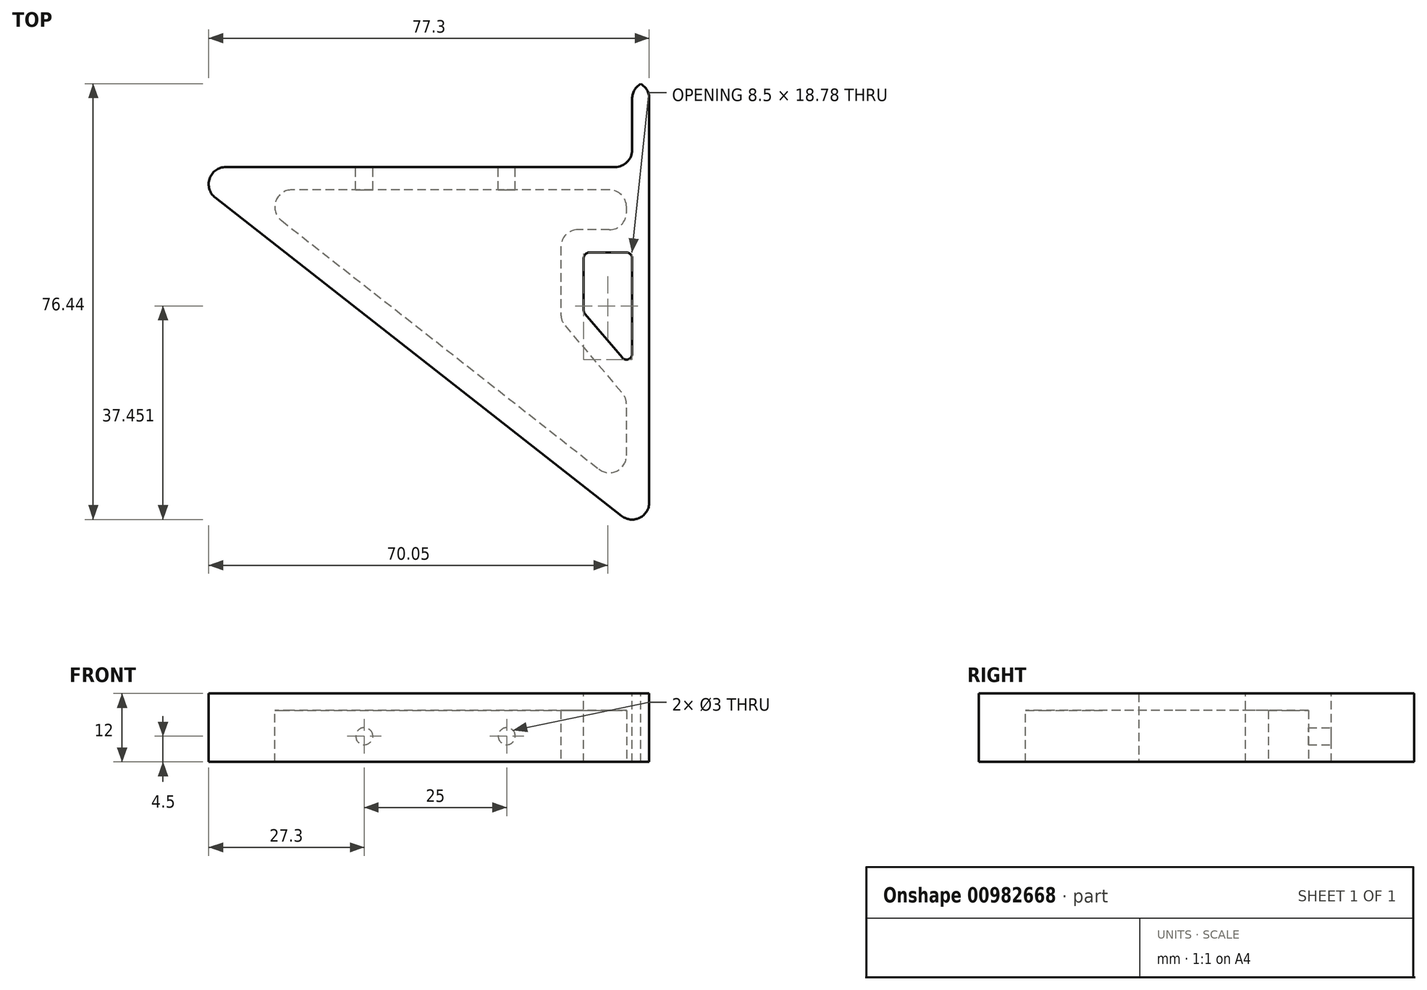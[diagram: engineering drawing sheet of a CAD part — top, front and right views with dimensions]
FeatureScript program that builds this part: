
annotation { "Feature Type Name" : "Feature", "Feature Type Description" : "" }
export const myFeature = defineFeature(function(context is Context, id is Id, definition is map)
    precondition{}
    {
        {
            var Q0;
            Q0=qCreatedBy(makeId("Top.planeOp"),FACE);
            var sketch = newSketch(context, id + "F0", { "sketchPlane" : qUnion([Q0])});
            skLineSegment(sketch, "E0", {"start": v(0, 0) * mm, "end": v(0, 80) * mm});
            skLineSegment(sketch, "E1", {"start": v(0, 80) * mm, "end": v(-3, 80) * mm});
            skLineSegment(sketch, "E2", {"start": v(-3, 80) * mm, "end": v(-3, 65) * mm});
            skLineSegment(sketch, "E3", {"start": v(-3, 65) * mm, "end": v(-83, 65) * mm});
            skLineSegment(sketch, "E4", {"start": v(-83, 65) * mm, "end": v(0, 0) * mm});
            skLineSegment(sketch, "E5", {"start": v(-3, 50) * mm, "end": v(-11.5, 50) * mm});
            skLineSegment(sketch, "E6", {"start": v(-11.5, 50) * mm, "end": v(-11.5, 39.5) * mm});
            skLineSegment(sketch, "E7", {"start": v(-11.5, 39.5) * mm, "end": v(-3, 29.5) * mm});
            skLineSegment(sketch, "E8", {"start": v(-3, 29.5) * mm, "end": v(-3, 50) * mm});
            skSolve(sketch);
        }
        {
            var Q0;
            Q0=makeQuery(id+"F0.imprint","IMPRINT",FACE,{"disambiguationData":[TD([[makeQuery(id+"F0.imprint","IMPRINT",EDGE,{"derivedFrom":sQuery(id+"F0.wireOp",EDGE,"E0")}),1.0]])]});
            extrude(context, id + "F1", {"entities" : qUnion([Q0]), "depth" : 12 * mm, "offsetDistance" : 25 * mm});
        }
        {
            var Q0;
            Q0=makeQuery(id+"F1.opExtrude","CAP_FACE",FACE,{"disambiguationData":[OSD([sQuery(id+"F0.wireOp",EDGE,"E0"),sQuery(id+"F0.wireOp",EDGE,"E1"),sQuery(id+"F0.wireOp",EDGE,"E2"),sQuery(id+"F0.wireOp",EDGE,"E3"),sQuery(id+"F0.wireOp",EDGE,"E4"),sQuery(id+"F0.wireOp",EDGE,"E5"),sQuery(id+"F0.wireOp",EDGE,"E6"),sQuery(id+"F0.wireOp",EDGE,"E7"),sQuery(id+"F0.wireOp",EDGE,"E8")])],"isStart":false});
            var sketch = newSketch(context, id + "F2", { "sketchPlane" : qUnion([Q0])});
            skLineSegment(sketch, "E9.0", {"start": v(-4, 61) * mm, "end": v(-71.4, 61) * mm});
            skLineSegment(sketch, "E10.0", {"start": v(-71.4, 61) * mm, "end": v(-4, 8.21) * mm});
            skLineSegment(sketch, "E11.0", {"start": v(-4, 54) * mm, "end": v(-15.5, 54) * mm});
            skLineSegment(sketch, "E12.0", {"start": v(-15.5, 54) * mm, "end": v(-15.5, 38.03) * mm});
            skLineSegment(sketch, "E13.0", {"start": v(-15.5, 38.03) * mm, "end": v(-4, 24.5) * mm});
            skLineSegment(sketch, "E14", {"start": v(-4, 54) * mm, "end": v(-4, 61) * mm});
            skLineSegment(sketch, "E15", {"start": v(-4, 8.21) * mm, "end": v(-4, 24.5) * mm});
            skSolve(sketch);
        }
        {
            var Q0;
            Q0=makeQuery(id+"F2.imprint","IMPRINT",FACE,{"disambiguationData":[TD([[makeQuery(id+"F2.imprint","IMPRINT",EDGE,{"derivedFrom":sQuery(id+"F2.wireOp",EDGE,"E9.0")}),1.0]])]});
            extrude(context, id + "F3", {"entities" : qUnion([Q0]), "operationType" : NewBodyOperationType.REMOVE, "oppositeDirection" : true, "depth" : 9 * mm, "offsetDistance" : 25 * mm});
        }
        {
            var Q0;
            Q0=makeQuery(id+"F1.opExtrude","SWEPT_FACE",FACE,{"disambiguationData":[OSD([sQuery(id+"F0.wireOp",EDGE,"E3")])]});
            var sketch = newSketch(context, id + "F4", { "sketchPlane" : qUnion([Q0])});
            skLineSegment(sketch, "E16", {"start": v(25, 7.5) * mm, "end": v(50, 7.5) * mm, "construction": true});
            skCircle(sketch, "E17", {"center": v(50, 7.5) * mm, "radius": 1.5 * mm});
            skCircle(sketch, "E18", {"center": v(25, 7.5) * mm, "radius": 1.5 * mm});
            skSolve(sketch);
        }
        {
            var Q0;
            Q0=qSketchRegion(id+"F4",true);
            extrude(context, id + "F5", {"entities" : qUnion([Q0]), "operationType" : NewBodyOperationType.REMOVE, "oppositeDirection" : true, "depth" : 4 * mm, "offsetDistance" : 25 * mm});
        }
        {
            var Q0;
            Q0=makeQuery(id+"F1.opExtrude","SWEPT_EDGE",EDGE,{"disambiguationData":[OSD([sQuery(id+"F0.wireOp",EDGE,"E2"),sQuery(id+"F0.wireOp",EDGE,"E3")])]});
            var Q1;
            Q1=makeQuery(id+"F3.boolean.opBoolean","COPY",EDGE,{"derivedFrom":makeQuery(id+"F3.opExtrude","SWEPT_EDGE",EDGE,{"disambiguationData":[OSD([sQuery(id+"F2.wireOp",EDGE,"E11.0"),sQuery(id+"F2.wireOp",EDGE,"E14")])]})});
            var Q2;
            Q2=makeQuery(id+"F3.boolean.opBoolean","COPY",EDGE,{"derivedFrom":makeQuery(id+"F3.opExtrude","SWEPT_EDGE",EDGE,{"disambiguationData":[OSD([sQuery(id+"F2.wireOp",EDGE,"E11.0"),sQuery(id+"F2.wireOp",EDGE,"E12.0")])]})});
            var Q3;
            Q3=makeQuery(id+"F3.boolean.opBoolean","COPY",EDGE,{"derivedFrom":makeQuery(id+"F3.opExtrude","SWEPT_EDGE",EDGE,{"disambiguationData":[OSD([sQuery(id+"F2.wireOp",EDGE,"E9.0"),sQuery(id+"F2.wireOp",EDGE,"E14")])]})});
            var Q4;
            Q4=makeQuery(id+"F3.boolean.opBoolean","COPY",EDGE,{"derivedFrom":makeQuery(id+"F3.opExtrude","SWEPT_EDGE",EDGE,{"disambiguationData":[OSD([sQuery(id+"F2.wireOp",EDGE,"E13.0"),sQuery(id+"F2.wireOp",EDGE,"E15")])]})});
            var Q5;
            Q5=makeQuery(id+"F3.boolean.opBoolean","COPY",EDGE,{"derivedFrom":makeQuery(id+"F3.opExtrude","SWEPT_EDGE",EDGE,{"disambiguationData":[OSD([sQuery(id+"F2.wireOp",EDGE,"E12.0"),sQuery(id+"F2.wireOp",EDGE,"E13.0")])]})});
            var Q6;
            Q6=makeQuery(id+"F3.boolean.opBoolean","COPY",EDGE,{"derivedFrom":makeQuery(id+"F3.opExtrude","SWEPT_EDGE",EDGE,{"disambiguationData":[OSD([sQuery(id+"F2.wireOp",EDGE,"E10.0"),sQuery(id+"F2.wireOp",EDGE,"E15")])]})});
            var Q7;
            Q7=makeQuery(id+"F3.boolean.opBoolean","COPY",EDGE,{"derivedFrom":makeQuery(id+"F3.opExtrude","SWEPT_EDGE",EDGE,{"disambiguationData":[OSD([sQuery(id+"F2.wireOp",EDGE,"E9.0"),sQuery(id+"F2.wireOp",EDGE,"E10.0")])]})});
            var Q8;
            Q8=makeQuery(id+"F1.opExtrude","SWEPT_EDGE",EDGE,{"disambiguationData":[OSD([sQuery(id+"F0.wireOp",EDGE,"E3"),sQuery(id+"F0.wireOp",EDGE,"E4")])]});
            var Q9;
            Q9=makeQuery(id+"F1.opExtrude","SWEPT_EDGE",EDGE,{"disambiguationData":[OSD([sQuery(id+"F0.wireOp",EDGE,"E1"),sQuery(id+"F0.wireOp",EDGE,"E2")])]});
            var Q10;
            Q10=makeQuery(id+"F1.opExtrude","SWEPT_EDGE",EDGE,{"disambiguationData":[OSD([sQuery(id+"F0.wireOp",EDGE,"E0"),sQuery(id+"F0.wireOp",EDGE,"E4")])]});
            var Q11;
            Q11=makeQuery(id+"F1.opExtrude","SWEPT_EDGE",EDGE,{"disambiguationData":[OSD([sQuery(id+"F0.wireOp",EDGE,"E0"),sQuery(id+"F0.wireOp",EDGE,"E1")])]});
            fillet(context, id + "F6", {"entities" : qUnion([Q0, Q1, Q2, Q3, Q4, Q5, Q6, Q7, Q8, Q9, Q10, Q11]), "radius" : 3 * mm, "tangentPropagation" : true, "allowEdgeOverflow" : false});
        }
        {
            var Q0;
            Q0=makeQuery(id+"F1.opExtrude","SWEPT_EDGE",EDGE,{"disambiguationData":[OSD([sQuery(id+"F0.wireOp",EDGE,"E5"),sQuery(id+"F0.wireOp",EDGE,"E6")])]});
            var Q1;
            Q1=makeQuery(id+"F1.opExtrude","SWEPT_EDGE",EDGE,{"disambiguationData":[OSD([sQuery(id+"F0.wireOp",EDGE,"E5"),sQuery(id+"F0.wireOp",EDGE,"E8")])]});
            var Q2;
            Q2=makeQuery(id+"F1.opExtrude","SWEPT_EDGE",EDGE,{"disambiguationData":[OSD([sQuery(id+"F0.wireOp",EDGE,"E6"),sQuery(id+"F0.wireOp",EDGE,"E7")])]});
            var Q3;
            Q3=makeQuery(id+"F1.opExtrude","SWEPT_EDGE",EDGE,{"disambiguationData":[OSD([sQuery(id+"F0.wireOp",EDGE,"E7"),sQuery(id+"F0.wireOp",EDGE,"E8")])]});
            fillet(context, id + "F7", {"entities" : qUnion([Q0, Q1, Q2, Q3]), "radius" : 1 * mm, "tangentPropagation" : true, "allowEdgeOverflow" : false});
        }
        {
            var Q0;
            Q0=makeQuery(id+"F1.opExtrude","SWEPT_BODY",BODY,{"disambiguationData":[OSD([sQuery(id+"F0.wireOp",EDGE,"E0"),sQuery(id+"F0.wireOp",EDGE,"E1"),sQuery(id+"F0.wireOp",EDGE,"E2"),sQuery(id+"F0.wireOp",EDGE,"E3"),sQuery(id+"F0.wireOp",EDGE,"E4"),sQuery(id+"F0.wireOp",EDGE,"E5"),sQuery(id+"F0.wireOp",EDGE,"E6"),sQuery(id+"F0.wireOp",EDGE,"E7"),sQuery(id+"F0.wireOp",EDGE,"E8")])]});
            var Q1;
            Q1=qCreatedBy(makeId("Top.planeOp"),FACE);
            mirror(context, id + "F8", {"entities" : qUnion([Q0]), "mirrorPlane" : qUnion([Q1])});
        }
        {
            var Q0;
            Q0=makeQuery(id+"F1.opExtrude","SWEPT_BODY",BODY,{"disambiguationData":[OSD([sQuery(id+"F0.wireOp",EDGE,"E0"),sQuery(id+"F0.wireOp",EDGE,"E1"),sQuery(id+"F0.wireOp",EDGE,"E2"),sQuery(id+"F0.wireOp",EDGE,"E3"),sQuery(id+"F0.wireOp",EDGE,"E4"),sQuery(id+"F0.wireOp",EDGE,"E5"),sQuery(id+"F0.wireOp",EDGE,"E6"),sQuery(id+"F0.wireOp",EDGE,"E7"),sQuery(id+"F0.wireOp",EDGE,"E8")])]});
            deleteBodies(context, id + "F9", {"entities" : qUnion([Q0])});
        }
    });
